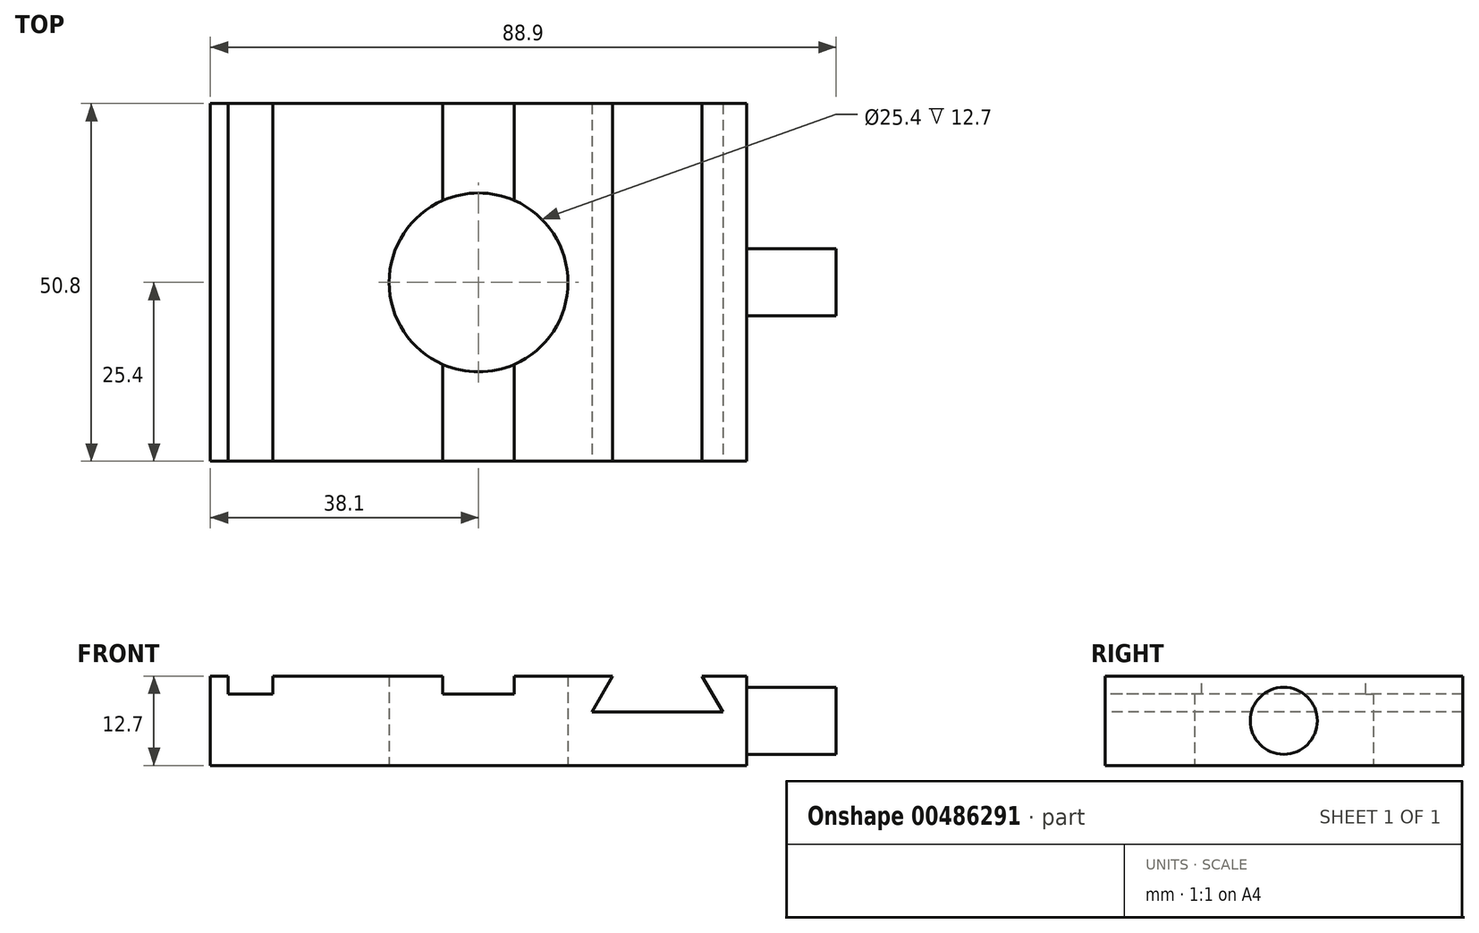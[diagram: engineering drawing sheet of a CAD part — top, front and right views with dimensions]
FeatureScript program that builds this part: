
annotation { "Feature Type Name" : "Feature", "Feature Type Description" : "" }
export const myFeature = defineFeature(function(context is Context, id is Id, definition is map)
    precondition{}
    {
        {
            var Q0;
            Q0=qCreatedBy(makeId("Top.planeOp"),FACE);
            var sketch = newSketch(context, id + "F0", { "sketchPlane" : qUnion([Q0])});
            skLineSegment(sketch, "E0.bottom", {"start": v(38.1, 25.4) * mm, "end": v(-38.1, 25.4) * mm});
            skLineSegment(sketch, "E0.top", {"start": v(38.1, -25.4) * mm, "end": v(-38.1, -25.4) * mm});
            skLineSegment(sketch, "E0.left", {"start": v(38.1, 25.4) * mm, "end": v(38.1, -25.4) * mm});
            skLineSegment(sketch, "E0.right", {"start": v(-38.1, 25.4) * mm, "end": v(-38.1, -25.4) * mm});
            skPoint(sketch, "E0.middle", {"position": v(0, 0) * mm});
            skCircle(sketch, "E1", {"center": v(0, 0) * mm, "radius": 12.7 * mm});
            skSolve(sketch);
        }
        {
            var Q0;
            Q0=makeQuery(id+"F0.imprint","IMPRINT",FACE,{"disambiguationData":[TD([[makeQuery(id+"F0.imprint","IMPRINT",EDGE,{"derivedFrom":sQuery(id+"F0.wireOp",EDGE,"E0.bottom")}),1.0]])]});
            extrude(context, id + "F1", {"entities" : qUnion([Q0]), "depth" : 12.7 * mm, "offsetDistance" : 25.4 * mm});
        }
        {
            var Q0;
            Q0=makeQuery(id+"F1.opExtrude","CAP_FACE",FACE,{"disambiguationData":[OSD([sQuery(id+"F0.wireOp",EDGE,"E0.bottom"),sQuery(id+"F0.wireOp",EDGE,"E0.top"),sQuery(id+"F0.wireOp",EDGE,"E0.left"),sQuery(id+"F0.wireOp",EDGE,"E0.right"),sQuery(id+"F0.wireOp",EDGE,"E1")])],"isStart":false});
            var sketch = newSketch(context, id + "F2", { "sketchPlane" : qUnion([Q0])});
            skLineSegment(sketch, "E2", {"start": v(-35.56, 25.4) * mm, "end": v(-35.56, -25.4) * mm});
            skLineSegment(sketch, "E3", {"start": v(-29.21, 25.4) * mm, "end": v(-29.2, -25.4) * mm});
            skLineSegment(sketch, "E4", {"start": v(-35.56, 25.4) * mm, "end": v(-29.21, 25.4) * mm});
            skLineSegment(sketch, "E5", {"start": v(-29.2, -25.4) * mm, "end": v(-35.56, -25.4) * mm});
            skLineSegment(sketch, "E6", {"start": v(-5.08, 25.4) * mm, "end": v(-5.08, -25.4) * mm});
            skLineSegment(sketch, "E7", {"start": v(5.08, 25.4) * mm, "end": v(5.08, -25.4) * mm});
            skLineSegment(sketch, "E8", {"start": v(-5.08, 25.4) * mm, "end": v(5.08, 25.4) * mm});
            skLineSegment(sketch, "E9", {"start": v(5.08, -25.4) * mm, "end": v(-5.08, -25.4) * mm});
            skLineSegment(sketch, "E10", {"start": v(0, 25.4) * mm, "end": v(0, -25.4) * mm, "construction": true});
            skPoint(sketch, "E11", {"position": v(0, 0) * mm});
            skSolve(sketch);
        }
        {
            var Q0;
            Q0=makeQuery(id+"F2.imprint","IMPRINT",FACE,{"disambiguationData":[TD([[makeQuery(id+"F2.imprint","IMPRINT",EDGE,{"derivedFrom":sQuery(id+"F2.wireOp",EDGE,"E2")}),1.0]])]});
            var Q1;
            {var subQ0=sQuery(id+"F2.wireOp",EDGE,"E8");Q1=makeQuery(id+"F2.imprint","IMPRINT",FACE,{"disambiguationData":[TD([[makeQuery(id+"F2.imprint","IMPRINT",EDGE,{"derivedFrom":subQ0}),1.0]])]});}
            var Q2;
            {var subQ0=sQuery(id+"F2.wireOp",EDGE,"E9");Q2=makeQuery(id+"F2.imprint","IMPRINT",FACE,{"disambiguationData":[TD([[makeQuery(id+"F2.imprint","IMPRINT",EDGE,{"derivedFrom":subQ0}),-1.0]])]});}
            extrude(context, id + "F3", {"entities" : qUnion([Q0, Q1, Q2]), "operationType" : NewBodyOperationType.REMOVE, "oppositeDirection" : true, "depth" : 2.54 * mm, "offsetDistance" : 25.4 * mm});
        }
        {
            var Q0;
            Q0=makeQuery(id+"F1.opExtrude","SWEPT_FACE",FACE,{"disambiguationData":[OSD([sQuery(id+"F0.wireOp",EDGE,"E0.top")])]});
            var sketch = newSketch(context, id + "F4", { "sketchPlane" : qUnion([Q0])});
            skLineSegment(sketch, "E12", {"start": v(34.68, 7.62) * mm, "end": v(31.75, 12.7) * mm});
            skLineSegment(sketch, "E13", {"start": v(34.68, 7.62) * mm, "end": v(16.12, 7.62) * mm});
            skLineSegment(sketch, "E14", {"start": v(16.12, 7.62) * mm, "end": v(19.05, 12.7) * mm});
            skLineSegment(sketch, "E15", {"start": v(19.05, 12.7) * mm, "end": v(31.75, 12.7) * mm});
            skLineSegment(sketch, "E16", {"start": v(25.4, 12.7) * mm, "end": v(25.4, 7.62) * mm, "construction": true});
            skSolve(sketch);
        }
        {
            var Q0;
            Q0=makeQuery(id+"F4.imprint","IMPRINT",FACE,{"disambiguationData":[TD([[makeQuery(id+"F4.imprint","IMPRINT",EDGE,{"derivedFrom":sQuery(id+"F4.wireOp",EDGE,"E12")}),1.0]])]});
            extrude(context, id + "F5", {"entities" : qUnion([Q0]), "operationType" : NewBodyOperationType.REMOVE, "endBound" : BoundingType.THROUGH_ALL, "oppositeDirection" : true, "depth" : 25.4 * mm, "offsetDistance" : 25.4 * mm});
        }
        {
            var Q0;
            Q0=makeQuery(id+"F1.opExtrude","SWEPT_FACE",FACE,{"disambiguationData":[OSD([sQuery(id+"F0.wireOp",EDGE,"E0.left")])]});
            var sketch = newSketch(context, id + "F6", { "sketchPlane" : qUnion([Q0])});
            skCircle(sketch, "E17", {"center": v(0, 6.35) * mm, "radius": 4.76 * mm});
            skPoint(sketch, "E17.centerSnap0", {"position": v(0, 12.7) * mm});
            skPoint(sketch, "E17.centerSnap1", {"position": v(-25.4, 6.35) * mm});
            skSolve(sketch);
        }
        {
            var Q0;
            Q0=makeQuery(id+"F6.imprint","IMPRINT",FACE,{"disambiguationData":[TD([[makeQuery(id+"F6.imprint","IMPRINT",EDGE,{"derivedFrom":sQuery(id+"F6.wireOp",EDGE,"E17")}),1.0]])]});
            extrude(context, id + "F7", {"entities" : qUnion([Q0]), "operationType" : NewBodyOperationType.ADD, "depth" : 12.7 * mm, "offsetDistance" : 25.4 * mm});
        }
    });
